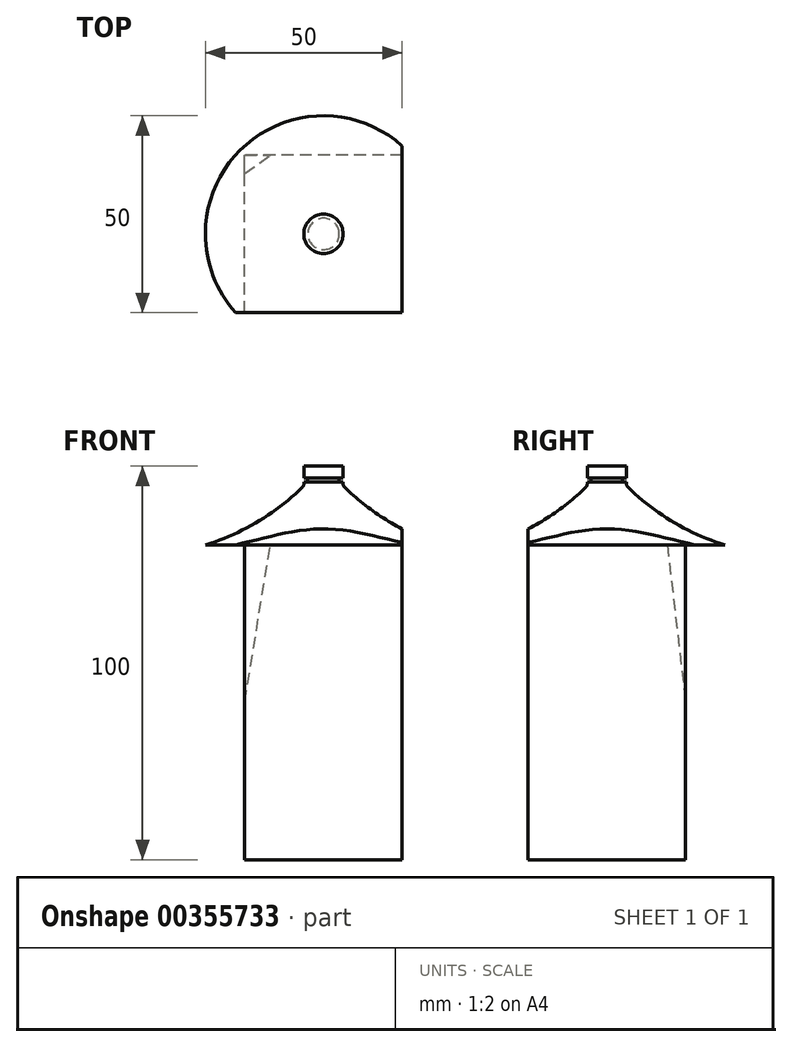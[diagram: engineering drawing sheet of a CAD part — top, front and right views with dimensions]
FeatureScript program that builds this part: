
annotation { "Feature Type Name" : "Feature", "Feature Type Description" : "" }
export const myFeature = defineFeature(function(context is Context, id is Id, definition is map)
    precondition{}
    {
        {
            var Q0;
            Q0=qCreatedBy(makeId("Front.planeOp"),FACE);
            var sketch = newSketch(context, id + "F0", { "sketchPlane" : qUnion([Q0])});
            skLineSegment(sketch, "E0.bottom", {"start": v(20, -40) * mm, "end": v(-20, -40) * mm});
            skLineSegment(sketch, "E0.top", {"start": v(20, 40) * mm, "end": v(-20, 40) * mm});
            skLineSegment(sketch, "E0.left", {"start": v(20, -40) * mm, "end": v(20, 40) * mm});
            skLineSegment(sketch, "E0.right", {"start": v(-20, -40) * mm, "end": v(-20, 40) * mm});
            skPoint(sketch, "E0.middle", {"position": v(0, 0) * mm});
            skSolve(sketch);
        }
        {
            var Q0;
            Q0=makeQuery(id+"F0.imprint","IMPRINT",FACE,{"disambiguationData":[TD([[makeQuery(id+"F0.imprint","IMPRINT",EDGE,{"derivedFrom":sQuery(id+"F0.wireOp",EDGE,"E0.bottom")}),-1.0]])]});
            extrude(context, id + "F1", {"entities" : qUnion([Q0]), "endBound" : BoundingType.SYMMETRIC, "depth" : 40 * mm});
        }
        {
            var Q0;
            Q0=makeQuery(id+"F1.opExtrude","SWEPT_FACE",FACE,{"disambiguationData":[OSD([sQuery(id+"F0.wireOp",EDGE,"E0.top")])]});
            var sketch = newSketch(context, id + "F2", { "sketchPlane" : qUnion([Q0])});
            skLineSegment(sketch, "E1", {"start": v(-20, 15.33) * mm, "end": v(-13.5, 20) * mm});
            skLineSegment(sketch, "E2.MirrorCS", {"start": v(20, 15.33) * mm, "end": v(13.5, 20) * mm});
            skLineSegment(sketch, "E3.MirrorCS", {"start": v(-20, -15.33) * mm, "end": v(-13.5, -20) * mm});
            skLineSegment(sketch, "E4.MirrorCS", {"start": v(20, -15.33) * mm, "end": v(13.5, -20) * mm});
            skSolve(sketch);
        }
        {
            var Q0;
            Q0=qCreatedBy(makeId("Top.planeOp"),FACE);
            var sketch = newSketch(context, id + "F3", { "sketchPlane" : qUnion([Q0])});
            skPoint(sketch, "E5.0", {"position": v(-20, 20) * mm});
            skPoint(sketch, "E6.0", {"position": v(20, 20) * mm});
            skSolve(sketch);
        }
        {
            var Q0;
            Q0=sQuery(id+"F2.wireOp",EDGE,"E1");
            var Q1;
            Q1=sQuery(id+"F3.wireOp",VERTEX,"E5.0");
            cPlane(context, id + "F4", {"entities" : qUnion([Q0, Q1]), "cplaneType" : CPlaneType.LINE_ANGLE, "offset" : 25 * mm, "angle" : 0 * degree, "width" : 150 * mm, "height" : 150 * mm});
        }
        {
            var Q0;
            Q0=qCreatedBy(id+"F4.planeOp",FACE);
            var sketch = newSketch(context, id + "F5", { "sketchPlane" : qUnion([Q0])});
            skLineSegment(sketch, "E7.0", {"start": v(4.72, 37.95) * mm, "end": v(-3.26, 37.4) * mm});
            skPoint(sketch, "E8.0", {"position": v(4.72, -2.32) * mm});
            skLineSegment(sketch, "E9", {"start": v(4.72, -2.32) * mm, "end": v(-3.26, 37.4) * mm});
            skLineSegment(sketch, "E10", {"start": v(4.72, 37.95) * mm, "end": v(4.72, -2.32) * mm});
            skSolve(sketch);
        }
        {
            var Q0;
            Q0 = qSketchRegion(id + "F5", true);
            extrude(context, id + "F6", {"entities" : qUnion([Q0]), "operationType" : NewBodyOperationType.REMOVE, "depth" : 25 * mm});
        }
        {
            var Q0;
            Q0=qCreatedBy(makeId("Front.planeOp"),FACE);
            var sketch = newSketch(context, id + "F7", { "sketchPlane" : qUnion([Q0])});
            skLineSegment(sketch, "E11", {"start": v(0, 40) * mm, "end": v(0, 60) * mm});
            skLineSegment(sketch, "E12", {"start": v(0, 60) * mm, "end": v(-5, 60) * mm});
            skLineSegment(sketch, "E13", {"start": v(-5, 60) * mm, "end": v(-5, 57) * mm});
            skLineSegment(sketch, "E14", {"start": v(-5, 57) * mm, "end": v(-4, 57) * mm});
            skLineSegment(sketch, "E15", {"start": v(-4, 57) * mm, "end": v(-4, 56) * mm});
            skLineSegment(sketch, "E16", {"start": v(-4, 56) * mm, "end": v(-5, 56) * mm});
            skLineSegment(sketch, "E17", {"start": v(-5, 56) * mm, "end": v(-5, 55.42) * mm});
            skPoint(sketch, "E18.visualSharp", {"position": v(-5, 59.31) * mm});
            skArc(sketch, "E19", {"start": v(-30, 40) * mm, "mid": v(-16.76, 45.85) * mm, "end": v(-5.3, 54.7) * mm});
            skLineSegment(sketch, "E20", {"start": v(0, 40) * mm, "end": v(-30, 40) * mm});
            skPoint(sketch, "E21.visualSharp", {"position": v(-5, 55) * mm});
            skArc(sketch, "E21.filletArc", {"start": v(-5.3, 54.7) * mm, "mid": v(-5.08, 55.03) * mm, "end": v(-5, 55.42) * mm});
            skSolve(sketch);
        }
        {
            var Q0;
            Q0=makeQuery(id+"F7.imprint","IMPRINT",FACE,{"disambiguationData":[TD([[makeQuery(id+"F7.imprint","IMPRINT",EDGE,{"derivedFrom":sQuery(id+"F7.wireOp",EDGE,"E11")}),1.0]])]});
            var Q1;
            Q1=sQuery(id+"F7.wireOp",EDGE,"E11");
            revolve(context, id + "F8", {"entities" : qUnion([Q0]), "axis" : qUnion([Q1]), "revolveType" : RevolveType.FULL});
        }
        {
            var Q0;
            Q0=makeQuery(id+"F1.opExtrude","CAP_FACE",FACE,{"disambiguationData":[OSD([sQuery(id+"F0.wireOp",EDGE,"E0.bottom"),sQuery(id+"F0.wireOp",EDGE,"E0.top"),sQuery(id+"F0.wireOp",EDGE,"E0.left"),sQuery(id+"F0.wireOp",EDGE,"E0.right")])],"isStart":false});
            var sketch = newSketch(context, id + "F9", { "sketchPlane" : qUnion([Q0])});
            skPoint(sketch, "E22.0", {"position": v(-13.5, 40) * mm});
            skPoint(sketch, "E23.0", {"position": v(13.5, 40) * mm});
            skArc(sketch, "E24", {"start": v(13.5, 40) * mm, "mid": v(0, 43.21) * mm, "end": v(-13.5, 40) * mm});
            skLineSegment(sketch, "E25", {"start": v(-13.5, 40) * mm, "end": v(13.5, 40) * mm});
            skSolve(sketch);
        }
        {
            var Q0;
            Q0=makeQuery(id+"F1.opExtrude","CAP_FACE",FACE,{"disambiguationData":[OSD([sQuery(id+"F0.wireOp",EDGE,"E0.bottom"),sQuery(id+"F0.wireOp",EDGE,"E0.top"),sQuery(id+"F0.wireOp",EDGE,"E0.left"),sQuery(id+"F0.wireOp",EDGE,"E0.right")])],"isStart":false});
            var sketch = newSketch(context, id + "F10", { "sketchPlane" : qUnion([Q0])});
            skLineSegment(sketch, "E26", {"start": v(-28.48, 27.08) * mm, "end": v(33.02, 27.08) * mm});
            skLineSegment(sketch, "E27", {"start": v(33.02, 27.08) * mm, "end": v(34.74, 67.52) * mm});
            skLineSegment(sketch, "E28", {"start": v(34.74, 67.52) * mm, "end": v(-45.03, 67.52) * mm});
            skLineSegment(sketch, "E29", {"start": v(-45.03, 67.52) * mm, "end": v(-28.48, 27.08) * mm});
            skSolve(sketch);
        }
        {
            var Q0;
            Q0 = qSketchRegion(id + "F10", true);
            extrude(context, id + "F11", {"entities" : qUnion([Q0]), "operationType" : NewBodyOperationType.REMOVE, "depth" : 25 * mm});
        }
        {
            var Q0;
            Q0=makeQuery(id+"F1.opExtrude","SWEPT_FACE",FACE,{"disambiguationData":[OSD([sQuery(id+"F0.wireOp",EDGE,"E0.left")])]});
            var sketch = newSketch(context, id + "F12", { "sketchPlane" : qUnion([Q0])});
            skLineSegment(sketch, "E30", {"start": v(-34.77, 21) * mm, "end": v(52.57, 20) * mm});
            skPoint(sketch, "E30.endSnap0", {"position": v(17.66, 20) * mm});
            skLineSegment(sketch, "E31", {"start": v(52.57, 20) * mm, "end": v(48.71, 61.13) * mm});
            skLineSegment(sketch, "E32", {"start": v(48.71, 61.13) * mm, "end": v(-45.79, 64.1) * mm});
            skLineSegment(sketch, "E33", {"start": v(-45.79, 64.1) * mm, "end": v(-34.77, 21) * mm});
            skSolve(sketch);
        }
        {
            var Q0;
            Q0 = qSketchRegion(id + "F12", true);
            extrude(context, id + "F13", {"entities" : qUnion([Q0]), "operationType" : NewBodyOperationType.REMOVE, "depth" : 25 * mm});
        }
    });
